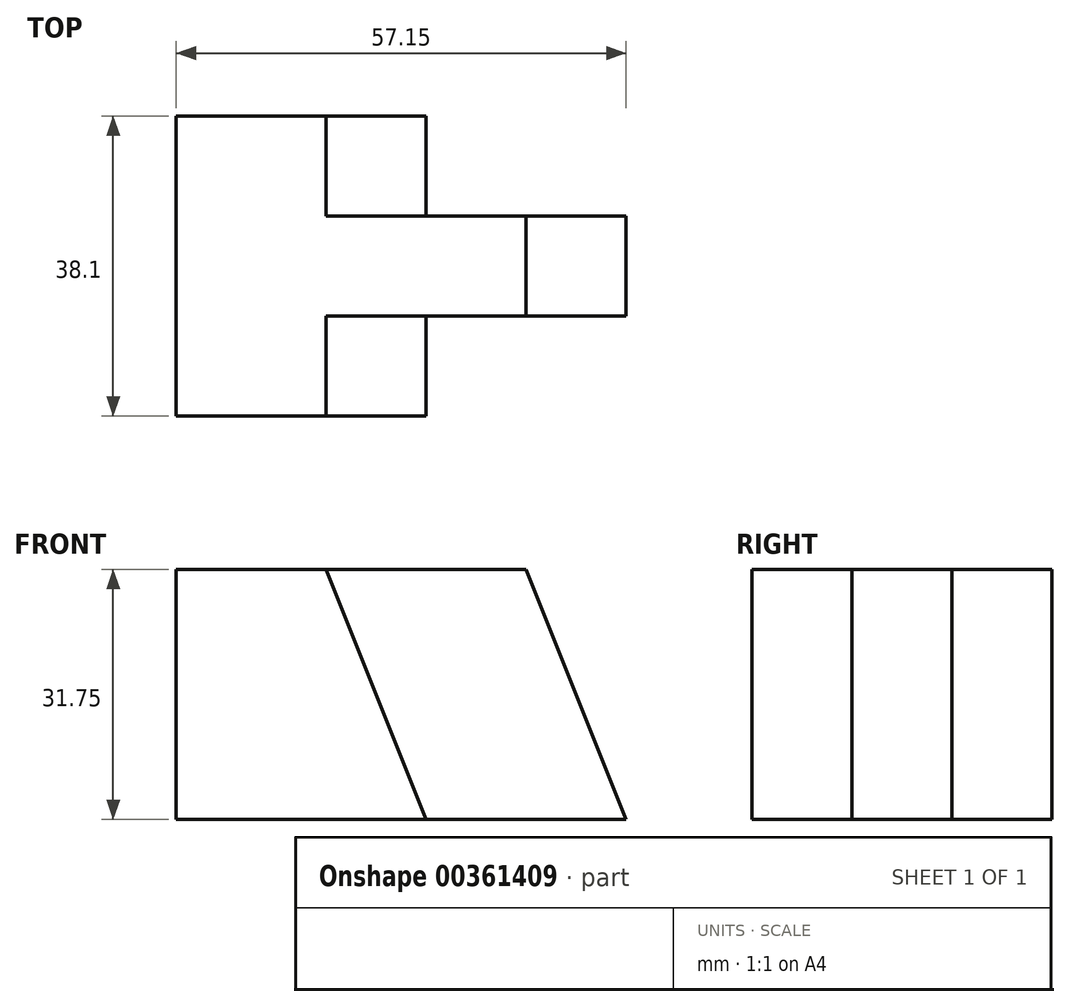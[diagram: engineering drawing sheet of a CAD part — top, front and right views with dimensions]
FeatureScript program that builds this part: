
annotation { "Feature Type Name" : "Feature", "Feature Type Description" : "" }
export const myFeature = defineFeature(function(context is Context, id is Id, definition is map)
    precondition{}
    {
        {
            var Q0;
            Q0=qCreatedBy(makeId("Top.planeOp"),FACE);
            var sketch = newSketch(context, id + "F0", { "sketchPlane" : qUnion([Q0])});
            skLineSegment(sketch, "E0", {"start": v(0, 0) * mm, "end": v(0, 38.1) * mm});
            skLineSegment(sketch, "E1", {"start": v(0, 38.1) * mm, "end": v(31.75, 38.1) * mm});
            skLineSegment(sketch, "E2", {"start": v(31.75, 38.1) * mm, "end": v(31.75, 25.4) * mm});
            skLineSegment(sketch, "E3", {"start": v(31.75, 25.4) * mm, "end": v(57.15, 25.4) * mm});
            skLineSegment(sketch, "E4", {"start": v(57.15, 25.4) * mm, "end": v(57.15, 12.7) * mm});
            skLineSegment(sketch, "E5", {"start": v(57.15, 12.7) * mm, "end": v(31.75, 12.7) * mm});
            skLineSegment(sketch, "E6", {"start": v(31.75, 12.7) * mm, "end": v(31.75, 0) * mm});
            skLineSegment(sketch, "E7", {"start": v(31.75, 0) * mm, "end": v(0, 0) * mm});
            skSolve(sketch);
        }
        {
            var Q0;
            Q0=makeQuery(id+"F0.imprint","IMPRINT",FACE,{"disambiguationData":[TD([[makeQuery(id+"F0.imprint","IMPRINT",EDGE,{"derivedFrom":sQuery(id+"F0.wireOp",EDGE,"E0")}),-1.0]])]});
            extrude(context, id + "F1", {"entities" : qUnion([Q0]), "depth" : 31.75 * mm});
        }
        {
            var Q0;
            Q0=makeQuery(id+"F1.opExtrude","SWEPT_FACE",FACE,{"disambiguationData":[OSD([sQuery(id+"F0.wireOp",EDGE,"E7")])]});
            var sketch = newSketch(context, id + "F2", { "sketchPlane" : qUnion([Q0])});
            skLineSegment(sketch, "E8", {"start": v(31.75, 0) * mm, "end": v(31.75, 31.75) * mm});
            skLineSegment(sketch, "E9", {"start": v(31.75, 31.75) * mm, "end": v(19.05, 31.75) * mm});
            skLineSegment(sketch, "E10", {"start": v(19.05, 31.75) * mm, "end": v(31.75, 0) * mm});
            skSolve(sketch);
        }
        {
            var Q0;
            Q0 = qSketchRegion(id + "F2", true);
            extrude(context, id + "F3", {"entities" : qUnion([Q0]), "operationType" : NewBodyOperationType.REMOVE, "oppositeDirection" : true, "depth" : 12.7 * mm});
        }
        {
            var Q0;
            Q0=makeQuery(id+"F1.opExtrude","SWEPT_FACE",FACE,{"disambiguationData":[OSD([sQuery(id+"F0.wireOp",EDGE,"E1")])]});
            var sketch = newSketch(context, id + "F4", { "sketchPlane" : qUnion([Q0])});
            skLineSegment(sketch, "E11", {"start": v(-31.75, 0) * mm, "end": v(-31.75, 31.75) * mm});
            skLineSegment(sketch, "E12", {"start": v(-31.75, 31.75) * mm, "end": v(-19.05, 31.75) * mm});
            skLineSegment(sketch, "E13", {"start": v(-19.05, 31.75) * mm, "end": v(-31.75, 0) * mm});
            skSolve(sketch);
        }
        {
            var Q0;
            Q0=makeQuery(id+"F4.imprint","IMPRINT",FACE,{"disambiguationData":[TD([[makeQuery(id+"F4.imprint","IMPRINT",EDGE,{"derivedFrom":sQuery(id+"F4.wireOp",EDGE,"E11")}),1.0]])]});
            extrude(context, id + "F5", {"entities" : qUnion([Q0]), "operationType" : NewBodyOperationType.REMOVE, "oppositeDirection" : true, "depth" : 12.7 * mm});
        }
        {
            var Q0;
            Q0=makeQuery(id+"F3.boolean.opBoolean","MERGE",FACE,{"derivedFrom":[makeQuery(id+"F1.opExtrude","SWEPT_FACE",FACE,{"disambiguationData":[OSD([sQuery(id+"F0.wireOp",EDGE,"E5")])]}),makeQuery(id+"F3.opExtrude","CAP_FACE",FACE,{"disambiguationData":[OSD([sQuery(id+"F2.wireOp",EDGE,"E8"),sQuery(id+"F2.wireOp",EDGE,"E9"),sQuery(id+"F2.wireOp",EDGE,"E10")])],"isStart":false})]});
            var sketch = newSketch(context, id + "F6", { "sketchPlane" : qUnion([Q0])});
            skLineSegment(sketch, "E14", {"start": v(57.15, 0) * mm, "end": v(57.15, 31.75) * mm});
            skLineSegment(sketch, "E15", {"start": v(57.15, 31.75) * mm, "end": v(44.45, 31.75) * mm});
            skLineSegment(sketch, "E16", {"start": v(44.45, 31.75) * mm, "end": v(57.15, 0) * mm});
            skSolve(sketch);
        }
        {
            var Q0;
            Q0 = qSketchRegion(id + "F6", true);
            extrude(context, id + "F7", {"entities" : qUnion([Q0]), "operationType" : NewBodyOperationType.REMOVE, "oppositeDirection" : true, "depth" : 12.7 * mm});
        }
    });
